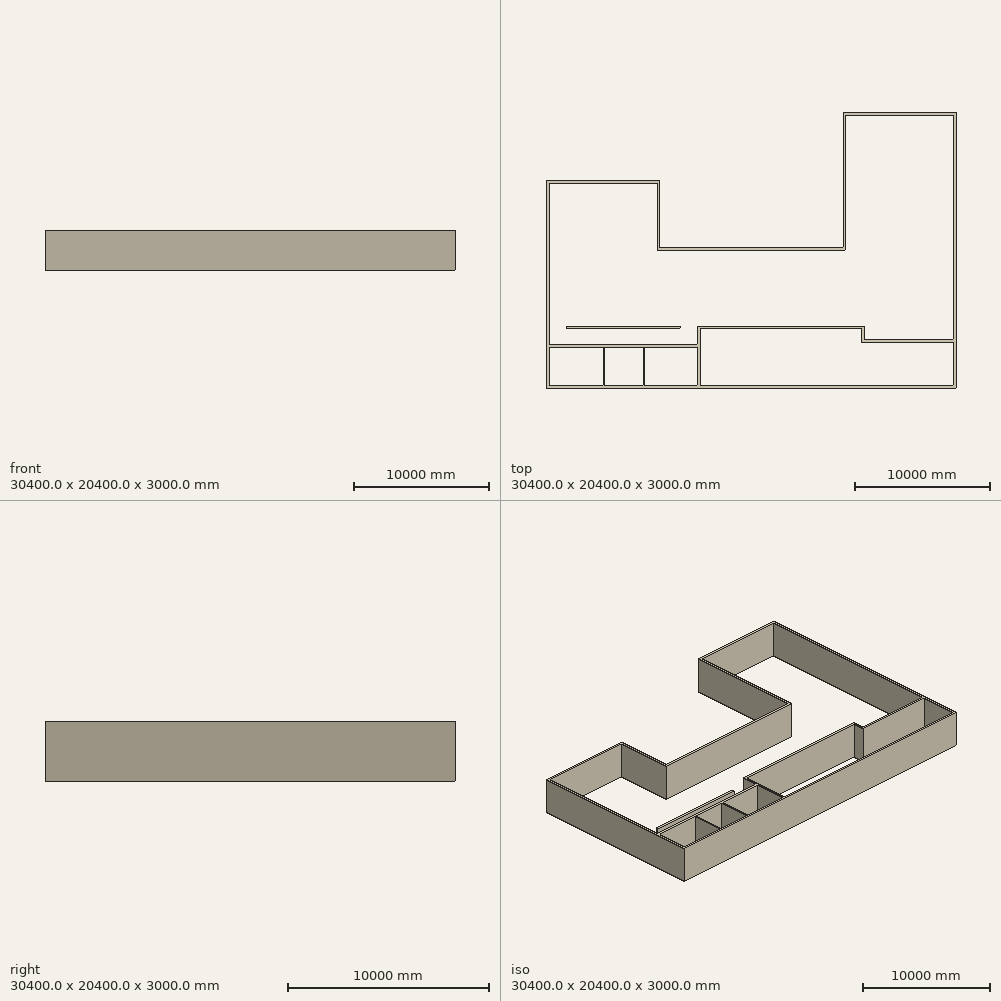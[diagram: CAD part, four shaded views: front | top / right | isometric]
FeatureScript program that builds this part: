
annotation { "Feature Type Name" : "Feature", "Feature Type Description" : "" }
export const myFeature = defineFeature(function(context is Context, id is Id, definition is map)
    precondition{}
    {
        {
            var Q0;
            Q0=qCreatedBy(makeId("Top.planeOp"),FACE);
            var sketch = newSketch(context, id + "F0", { "sketchPlane" : qUnion([Q0])});
            skLineSegment(sketch, "E0.bottom", {"start": v(15000, -10000) * mm, "end": v(-3800, -10000) * mm});
            skLineSegment(sketch, "E0.top", {"start": v(15000, 10000) * mm, "end": v(7000, 10000) * mm});
            skLineSegment(sketch, "E0.left", {"start": v(15000, -10000) * mm, "end": v(15000, -6800) * mm});
            skLineSegment(sketch, "E0.right", {"start": v(-15000, -10000) * mm, "end": v(-15000, -7200) * mm});
            skPoint(sketch, "E0.middle", {"position": v(0, 0) * mm});
            skLineSegment(sketch, "E1", {"start": v(7000, 10000) * mm, "end": v(7000, 0) * mm});
            skLineSegment(sketch, "E2", {"start": v(7000, 0) * mm, "end": v(-7000, 0) * mm});
            skLineSegment(sketch, "E3", {"start": v(-7000, 0) * mm, "end": v(-7000, 5000) * mm});
            skLineSegment(sketch, "E4", {"start": v(-15000, 5000) * mm, "end": v(-7000, 5000) * mm});
            skLineSegment(sketch, "E5", {"start": v(-15000, -7000) * mm, "end": v(-11000, -7000) * mm});
            skLineSegment(sketch, "E6", {"start": v(-11000, -7200) * mm, "end": v(-11000, -10000) * mm});
            skLineSegment(sketch, "E7", {"start": v(-11000, -7000) * mm, "end": v(-8000, -7000) * mm});
            skLineSegment(sketch, "E8", {"start": v(-8000, -7200) * mm, "end": v(-8000, -10000) * mm});
            skLineSegment(sketch, "E9", {"start": v(-8000, -7000) * mm, "end": v(-4000, -7000) * mm});
            skLineSegment(sketch, "E10", {"start": v(-4000, -7200) * mm, "end": v(-4000, -10000) * mm});
            skLineSegment(sketch, "E11.bottom", {"start": v(-5250, -5800) * mm, "end": v(-13750, -5800) * mm});
            skLineSegment(sketch, "E11.top", {"start": v(-5250, -5600) * mm, "end": v(-13750, -5600) * mm});
            skLineSegment(sketch, "E11.left", {"start": v(-5250, -5800) * mm, "end": v(-5250, -5600) * mm});
            skLineSegment(sketch, "E11.right", {"start": v(-13750, -5800) * mm, "end": v(-13750, -5600) * mm});
            skPoint(sketch, "E11.middle", {"position": v(-9500, -5700) * mm});
            skPoint(sketch, "E11.middle.positionSnap0", {"position": v(-9500, -7000) * mm});
            skPoint(sketch, "E11.centerSnap0", {"position": v(-9500, -7000) * mm});
            skLineSegment(sketch, "E12", {"start": v(-4000, -7000) * mm, "end": v(-4000, -5600) * mm});
            skLineSegment(sketch, "E13", {"start": v(-4000, -5600) * mm, "end": v(8370.93, -5600) * mm});
            skLineSegment(sketch, "E14", {"start": v(10000, -6600) * mm, "end": v(15000, -6600) * mm});
            skArc(sketch, "E15", {"start": v(13432.87, -628.7) * mm, "mid": v(10554.95, -1705.82) * mm, "end": v(8801.5, -4229.32) * mm});
            skArc(sketch, "E16", {"start": v(13461.16, -1698.06) * mm, "mid": v(11256.33, -2502.33) * mm, "end": v(9860.23, -4388.86) * mm});
            skLineSegment(sketch, "E17", {"start": v(10000, -6600) * mm, "end": v(8370.93, -6600) * mm});
            skLineSegment(sketch, "E18", {"start": v(8370.93, -6600) * mm, "end": v(8370.93, -5600) * mm});
            skLineSegment(sketch, "E19", {"start": v(9040, -4554.29) * mm, "end": v(9624.98, -4554.29) * mm});
            skLineSegment(sketch, "E20", {"start": v(13696.72, -878.3) * mm, "end": v(13696.72, -1448.48) * mm});
            skLineSegment(sketch, "E21.0", {"start": v(15200, -10200) * mm, "end": v(15200, 10200) * mm});
            skLineSegment(sketch, "E21.1", {"start": v(15200, -10200) * mm, "end": v(-15200, -10200) * mm});
            skLineSegment(sketch, "E21.2", {"start": v(15200, 10200) * mm, "end": v(6800, 10200) * mm});
            skLineSegment(sketch, "E21.3", {"start": v(-15200, -10200) * mm, "end": v(-15200, 5200) * mm});
            skLineSegment(sketch, "E21.4", {"start": v(6800, 10200) * mm, "end": v(6800, 200) * mm});
            skLineSegment(sketch, "E21.5", {"start": v(6800, 200) * mm, "end": v(-6800, 200) * mm});
            skLineSegment(sketch, "E21.6", {"start": v(-6800, 200) * mm, "end": v(-6800, 5200) * mm});
            skLineSegment(sketch, "E21.7", {"start": v(-15200, 5200) * mm, "end": v(-6800, 5200) * mm});
            skLineSegment(sketch, "E22.0", {"start": v(-3800, -7000) * mm, "end": v(-3800, -10000) * mm});
            skLineSegment(sketch, "E23.0", {"start": v(-3800, -7000) * mm, "end": v(-3800, -5800) * mm});
            skLineSegment(sketch, "E24.0", {"start": v(10000, -6800) * mm, "end": v(15000, -6800) * mm});
            skLineSegment(sketch, "E24.1", {"start": v(10000, -6800) * mm, "end": v(8170.93, -6800) * mm});
            skLineSegment(sketch, "E24.2", {"start": v(8170.93, -6800) * mm, "end": v(8170.93, -5800) * mm});
            skLineSegment(sketch, "E24.3", {"start": v(-3800, -5800) * mm, "end": v(8170.93, -5800) * mm});
            skLineSegment(sketch, "E25", {"start": v(-15000, -7200) * mm, "end": v(-4000, -7200) * mm});
            skLineSegment(sketch, "E26", {"start": v(-10910, -7200) * mm, "end": v(-10910, -10000) * mm});
            skLineSegment(sketch, "E27", {"start": v(-7910, -7200) * mm, "end": v(-7910, -10000) * mm});
            skPoint(sketch, "E28.newPointA", {"position": v(8700, -4600) * mm});
            skArc(sketch, "E28.filletArc", {"start": v(8801.5, -4229.32) * mm, "mid": v(8838.45, -4452.2) * mm, "end": v(9040, -4554.29) * mm});
            skPoint(sketch, "E29.visualSharp", {"position": v(9804.73, -4554.29) * mm});
            skArc(sketch, "E29.filletArc", {"start": v(9624.98, -4554.29) * mm, "mid": v(9768.77, -4508.8) * mm, "end": v(9860.23, -4388.86) * mm});
            skPoint(sketch, "E30.visualSharp", {"position": v(13696.72, -620.82) * mm});
            skArc(sketch, "E30.filletArc", {"start": v(13696.72, -878.3) * mm, "mid": v(13618.53, -696.7) * mm, "end": v(13432.87, -628.7) * mm});
            skPoint(sketch, "E31.visualSharp", {"position": v(13696.72, -1691.25) * mm});
            skArc(sketch, "E31.filletArc", {"start": v(13461.16, -1698.06) * mm, "mid": v(13628.53, -1620.08) * mm, "end": v(13696.72, -1448.48) * mm});
            skLineSegment(sketch, "E32.bottom", {"start": v(15000, 3046.25) * mm, "end": v(14000, 3046.25) * mm});
            skLineSegment(sketch, "E32.top", {"start": v(15000, 4446.25) * mm, "end": v(14000, 4446.25) * mm});
            skLineSegment(sketch, "E32.left", {"start": v(15000, 3046.25) * mm, "end": v(15000, 4446.25) * mm});
            skLineSegment(sketch, "E32.right", {"start": v(14000, 3046.25) * mm, "end": v(14000, 4446.25) * mm});
            skLineSegment(sketch, "E33.bottom", {"start": v(15200, 0) * mm, "end": v(21200, 0) * mm});
            skLineSegment(sketch, "E33.top", {"start": v(15200, 3000) * mm, "end": v(21200, 3000) * mm});
            skLineSegment(sketch, "E33.left", {"start": v(15200, 0) * mm, "end": v(15200, 3000) * mm});
            skLineSegment(sketch, "E33.right", {"start": v(21200, 0) * mm, "end": v(21200, 3000) * mm});
            skLineSegment(sketch, "E34.trimOffspring", {"start": v(-4000, -10000) * mm, "end": v(-15000, -10000) * mm});
            skLineSegment(sketch, "E35.trimOffspring", {"start": v(-15000, -7000) * mm, "end": v(-15000, 5000) * mm});
            skLineSegment(sketch, "E36.trimOffspring", {"start": v(15000, -6600) * mm, "end": v(15000, 10000) * mm});
            skSolve(sketch);
        }
        {
            var Q0;
            Q0=makeQuery(id+"F0.imprint","IMPRINT",FACE,{"disambiguationData":[TD([[makeQuery(id+"F0.imprint","IMPRINT",EDGE,{"derivedFrom":sQuery(id+"F0.wireOp",EDGE,"E0.bottom")}),1.0]])]});
            extrude(context, id + "F1", {"entities" : qUnion([Q0]), "depth" : 3000 * mm, "offsetDistance" : 25 * mm});
        }
        {
            var Q0;
            Q0=makeQuery(id+"F0.imprint","IMPRINT",FACE,{"disambiguationData":[TD([[makeQuery(id+"F0.imprint","IMPRINT",EDGE,{"derivedFrom":sQuery(id+"F0.wireOp",EDGE,"E11.bottom")}),-1.0]])]});
            extrude(context, id + "F2", {"entities" : qUnion([Q0]), "depth" : 2400 * mm, "offsetDistance" : 25 * mm});
        }
        {
            var Q0;
            {var subQ0=sQuery(id+"F0.wireOp",EDGE,"E8");Q0=makeQuery(id+"F0.imprint","IMPRINT",FACE,{"disambiguationData":[TD([[makeQuery(id+"F0.imprint","IMPRINT",EDGE,{"derivedFrom":subQ0}),1.0]])]});}
            var Q1;
            {var subQ0=sQuery(id+"F0.wireOp",EDGE,"E6");Q1=makeQuery(id+"F0.imprint","IMPRINT",FACE,{"disambiguationData":[TD([[makeQuery(id+"F0.imprint","IMPRINT",EDGE,{"derivedFrom":subQ0}),1.0]])]});}
            extrude(context, id + "F3", {"entities" : qUnion([Q0, Q1]), "operationType" : NewBodyOperationType.ADD, "depth" : 3000 * mm, "offsetDistance" : 25 * mm});
        }
    });
